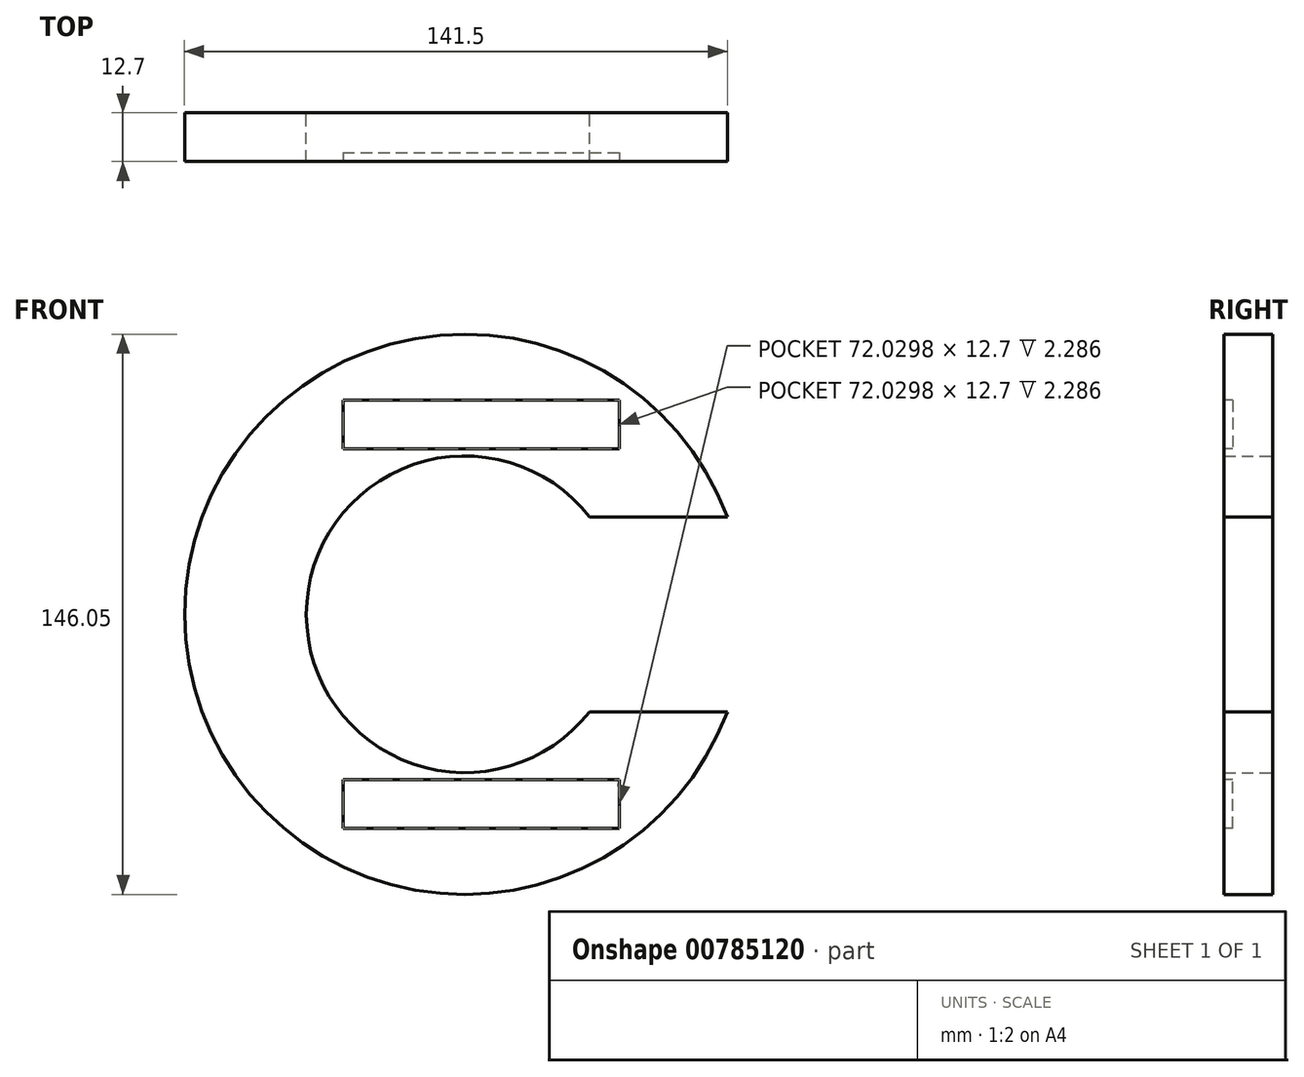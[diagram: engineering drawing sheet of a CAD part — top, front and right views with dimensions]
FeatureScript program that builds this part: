
annotation { "Feature Type Name" : "Feature", "Feature Type Description" : "" }
export const myFeature = defineFeature(function(context is Context, id is Id, definition is map)
    precondition{}
    {
        {
            var Q0;
            Q0=qCreatedBy(makeId("Front.planeOp"),FACE);
            var sketch = newSketch(context, id + "F0", { "sketchPlane" : qUnion([Q0])});
            skCircle(sketch, "E0", {"center": v(0, 0) * mm, "radius": 73.03 * mm});
            skCircle(sketch, "E1", {"center": v(0, 0) * mm, "radius": 41.28 * mm});
            skLineSegment(sketch, "E2", {"start": v(32.53, 25.4) * mm, "end": v(68.47, 25.4) * mm});
            skLineSegment(sketch, "E3.MirrorCS", {"start": v(32.53, -25.4) * mm, "end": v(68.47, -25.4) * mm});
            skSolve(sketch);
        }
        {
            var Q0;
            {var subQ0=sQuery(id+"F0.wireOp",EDGE,"E2");Q0=makeQuery(id+"F0.imprint","IMPRINT",FACE,{"disambiguationData":[TD([[makeQuery(id+"F0.imprint","IMPRINT",EDGE,{"derivedFrom":subQ0}),1.0]])]});}
            extrude(context, id + "F1", {"entities" : qUnion([Q0]), "depth" : 12.7 * mm, "offsetDistance" : 25.4 * mm});
        }
        {
            var Q0;
            Q0=makeQuery(id+"F1.opExtrude","CAP_FACE",FACE,{"disambiguationData":[OSD([sQuery(id+"F0.wireOp",EDGE,"E0"),sQuery(id+"F0.wireOp",EDGE,"E1"),sQuery(id+"F0.wireOp",EDGE,"E2"),sQuery(id+"F0.wireOp",EDGE,"E3.MirrorCS")])],"isStart":false});
            var sketch = newSketch(context, id + "F2", { "sketchPlane" : qUnion([Q0])});
            skLineSegment(sketch, "E4.bottom", {"start": v(-31.72, 55.8) * mm, "end": v(40.31, 55.8) * mm});
            skLineSegment(sketch, "E4.top", {"start": v(-31.72, 43.1) * mm, "end": v(40.31, 43.1) * mm});
            skLineSegment(sketch, "E4.left", {"start": v(-31.72, 55.8) * mm, "end": v(-31.72, 43.1) * mm});
            skLineSegment(sketch, "E4.right", {"start": v(40.31, 55.8) * mm, "end": v(40.31, 43.1) * mm});
            skLineSegment(sketch, "E5.MirrorCS", {"start": v(-31.72, -43.1) * mm, "end": v(40.31, -43.1) * mm});
            skLineSegment(sketch, "E6.MirrorCS", {"start": v(-31.72, -55.8) * mm, "end": v(-31.72, -43.1) * mm});
            skLineSegment(sketch, "E7.MirrorCS", {"start": v(-31.72, -55.8) * mm, "end": v(40.31, -55.8) * mm});
            skLineSegment(sketch, "E8.MirrorCS", {"start": v(40.31, -55.8) * mm, "end": v(40.31, -43.1) * mm});
            skSolve(sketch);
        }
        {
            var Q0;
            Q0 = qSketchRegion(id + "F2", true);
            extrude(context, id + "F3", {"entities" : qUnion([Q0]), "operationType" : NewBodyOperationType.REMOVE, "oppositeDirection" : true, "depth" : 2.3 * mm, "offsetDistance" : 25.4 * mm});
        }
    });
